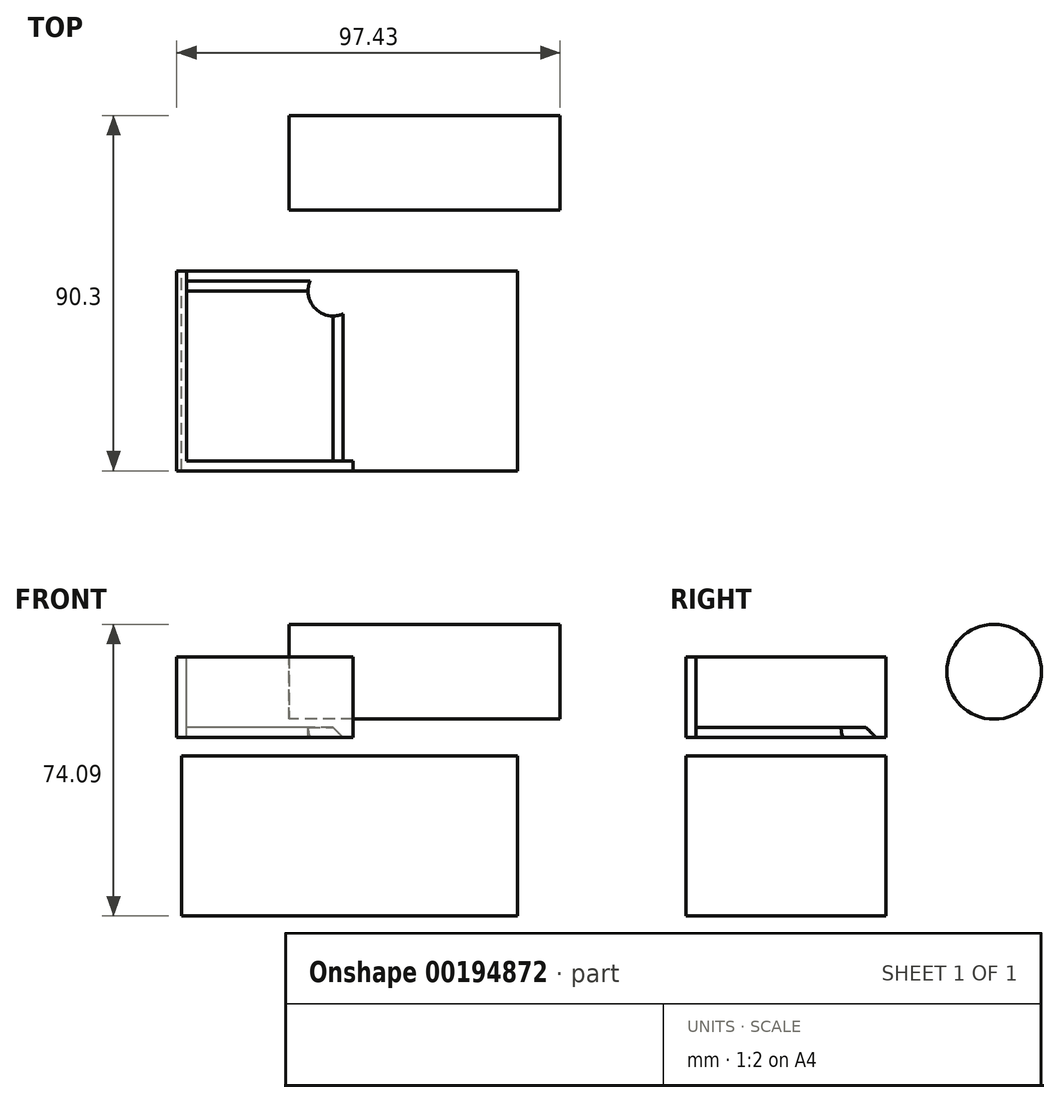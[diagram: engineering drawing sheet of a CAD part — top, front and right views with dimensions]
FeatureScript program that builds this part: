
annotation { "Feature Type Name" : "Feature", "Feature Type Description" : "" }
export const myFeature = defineFeature(function(context is Context, id is Id, definition is map)
    precondition{}
    {
        {
            var Q0;
            Q0=qCreatedBy(makeId("Front.planeOp"),FACE);
            var sketch = newSketch(context, id + "F0", { "sketchPlane" : qUnion([Q0])});
            skLineSegment(sketch, "E0.bottom", {"start": v(-52.74, -7.47) * mm, "end": v(32.58, -7.47) * mm});
            skLineSegment(sketch, "E0.top", {"start": v(-52.74, -48.15) * mm, "end": v(32.58, -48.15) * mm});
            skLineSegment(sketch, "E0.left", {"start": v(-52.74, -7.47) * mm, "end": v(-52.74, -48.15) * mm});
            skLineSegment(sketch, "E0.right", {"start": v(32.58, -7.47) * mm, "end": v(32.58, -48.15) * mm});
            skLineSegment(sketch, "E1.bottom", {"start": v(-9.18, -2.79) * mm, "end": v(-54, -2.79) * mm});
            skLineSegment(sketch, "E1.top", {"start": v(-9.18, 17.73) * mm, "end": v(-54, 17.73) * mm});
            skLineSegment(sketch, "E1.left", {"start": v(-9.18, -2.79) * mm, "end": v(-9.18, 17.73) * mm});
            skLineSegment(sketch, "E1.right", {"start": v(-54, -2.79) * mm, "end": v(-54, 17.73) * mm});
            skSolve(sketch);
        }
        {
            var Q0;
            Q0 = qSketchRegion(id + "F0", true);
            extrude(context, id + "F1", {"entities" : qUnion([Q0]), "depth" : 50.8 * mm});
        }
        {
            var Q0;
            Q0=makeQuery(id+"F1.opExtrude","SWEPT_FACE",FACE,{"disambiguationData":[OSD([sQuery(id+"F0.wireOp",EDGE,"E1.top")])]});
            var Q1;
            Q1=makeQuery(id+"F1.opExtrude","CAP_FACE",FACE,{"disambiguationData":[OSD([sQuery(id+"F0.wireOp",EDGE,"E1.bottom"),sQuery(id+"F0.wireOp",EDGE,"E1.top"),sQuery(id+"F0.wireOp",EDGE,"E1.left"),sQuery(id+"F0.wireOp",EDGE,"E1.right")])],"isStart":true});
            var Q2;
            Q2=makeQuery(id+"F1.opExtrude","SWEPT_FACE",FACE,{"disambiguationData":[OSD([sQuery(id+"F0.wireOp",EDGE,"E1.left")])]});
            shell(context, id + "F2", {"entities" : qUnion([Q0, Q1, Q2]), "thickness" : 2.54 * mm});
        }
        {
            var Q0;
            {var subQ0=sQuery(id+"F0.wireOp",EDGE,"E1.bottom");Q0=makeQuery(id+"F2.opShell","OFFSET_EDGE",EDGE,{"disambiguationData":[OSD([subQ0]),TDD([makeQuery(id+"F1.opExtrude","CAP_EDGE",EDGE,{"disambiguationData":[OSD([subQ0])],"isStart":true})])]});}
            var Q1;
            Q1=makeQuery(id+"F2.opShell","OFFSET_EDGE",EDGE,{"disambiguationData":[OSD([sQuery(id+"F0.wireOp",EDGE,"E1.bottom"),sQuery(id+"F0.wireOp",EDGE,"E1.left")])]});
            chamfer(context, id + "F3", {"entities" : qUnion([Q0, Q1]), "width" : 5.08 * mm, "tangentPropagation" : true});
        }
        {
            var Q0;
            Q0=makeQuery(id+"F2.opShell","OFFSET_FACE",FACE,{"disambiguationData":[OSD([sQuery(id+"F0.wireOp",EDGE,"E1.bottom")])]});
            var sketch = newSketch(context, id + "F4", { "sketchPlane" : qUnion([Q0])});
            skCircle(sketch, "E2", {"center": v(-14.26, -5.08) * mm, "radius": 6.8 * mm});
            skSolve(sketch);
        }
        {
            var Q0;
            Q0=sQuery(id+"F4.wireOp",VERTEX,"E2.center");
            var Q1;
            Q1=makeQuery(id+"F1.opExtrude","SWEPT_BODY",BODY,{"disambiguationData":[OSD([sQuery(id+"F0.wireOp",EDGE,"E1.bottom"),sQuery(id+"F0.wireOp",EDGE,"E1.top"),sQuery(id+"F0.wireOp",EDGE,"E1.left"),sQuery(id+"F0.wireOp",EDGE,"E1.right")])]});
            hole(context, id + "F5", {"style" : HoleStyle.SIMPLE, "endStyle" : HoleEndStyle.THROUGH, "holeDiameter" : 12.7 * mm, "locations" : qUnion([Q0]), "scope" : qUnion([Q1]), "isTappedThrough" : true});
        }
        {
            var Q0;
            Q0=qCreatedBy(makeId("Right.planeOp"),FACE);
            var sketch = newSketch(context, id + "F6", { "sketchPlane" : qUnion([Q0])});
            skCircle(sketch, "E3", {"center": v(27.46, 13.9) * mm, "radius": 12.04 * mm});
            skSolve(sketch);
        }
        {
            var Q0;
            Q0=makeQuery(id+"F6.imprint","IMPRINT",FACE,{"disambiguationData":[TD([[makeQuery(id+"F6.imprint","IMPRINT",EDGE,{"derivedFrom":sQuery(id+"F6.wireOp",EDGE,"E3")}),1.0]])]});
            extrude(context, id + "F7", {"entities" : qUnion([Q0]), "depth" : 43.43 * mm, "hasSecondDirection" : true, "secondDirectionOppositeDirection" : true, "secondDirectionDepth" : 25.4 * mm});
        }
    });
